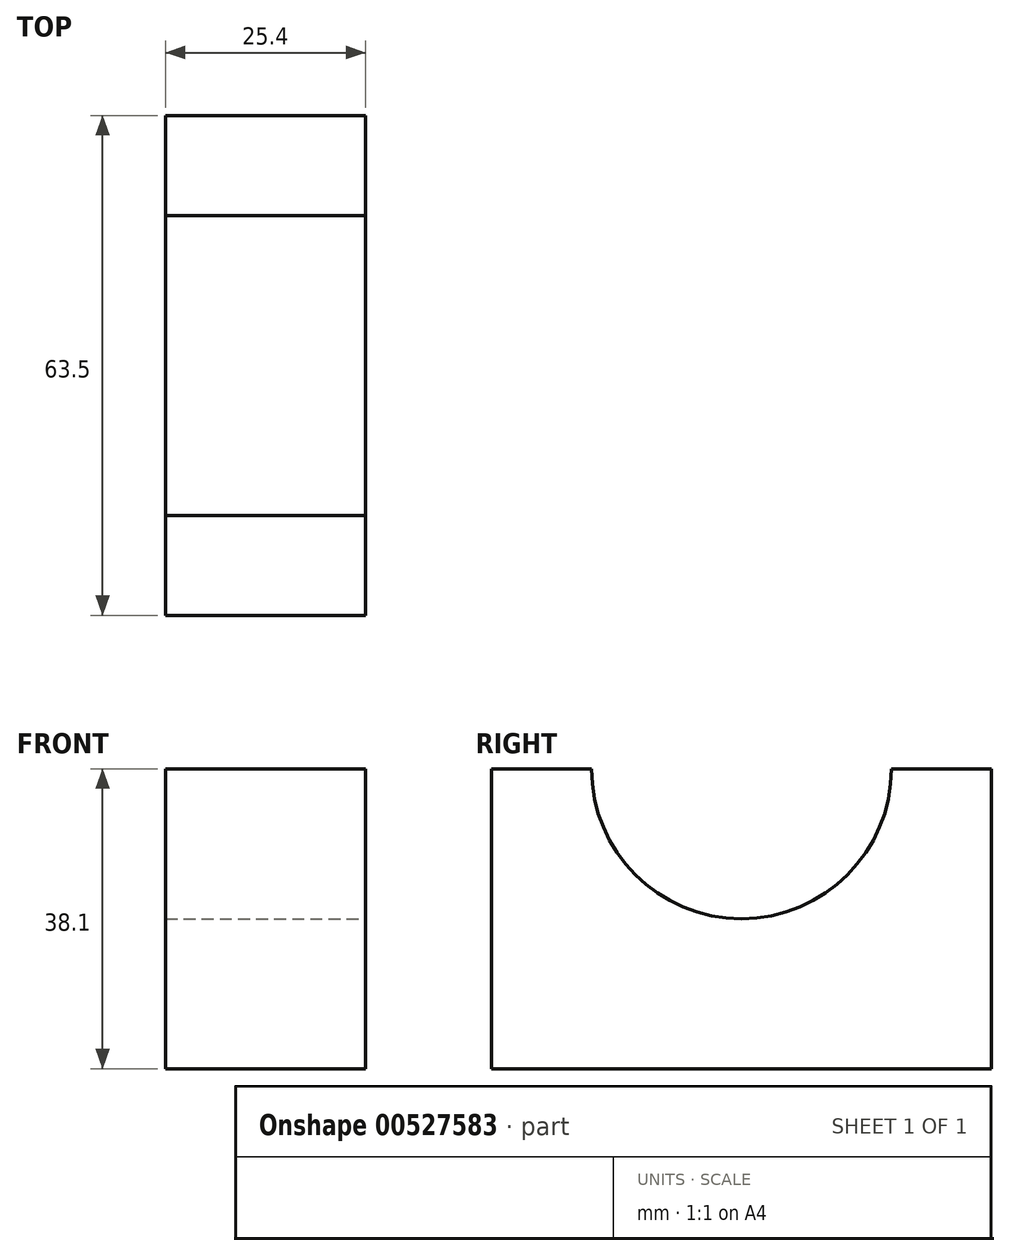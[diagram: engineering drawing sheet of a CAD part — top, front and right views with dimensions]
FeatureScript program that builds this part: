
annotation { "Feature Type Name" : "Feature", "Feature Type Description" : "" }
export const myFeature = defineFeature(function(context is Context, id is Id, definition is map)
    precondition{}
    {
        {
            var Q0;
            Q0=qCreatedBy(makeId("Front.planeOp"),FACE);
            var sketch = newSketch(context, id + "F0", { "sketchPlane" : qUnion([Q0])});
            skLineSegment(sketch, "E0", {"start": v(0, 0) * mm, "end": v(25.4, 0) * mm});
            skLineSegment(sketch, "E1", {"start": v(25.4, 0) * mm, "end": v(25.4, 38.1) * mm});
            skLineSegment(sketch, "E2", {"start": v(25.4, 38.1) * mm, "end": v(0, 38.1) * mm});
            skLineSegment(sketch, "E3", {"start": v(0, 38.1) * mm, "end": v(0, 0) * mm});
            skSolve(sketch);
        }
        {
            var Q0;
            Q0=makeQuery(id+"F0.imprint","IMPRINT",FACE,{"disambiguationData":[TD([[makeQuery(id+"F0.imprint","IMPRINT",EDGE,{"derivedFrom":sQuery(id+"F0.wireOp",EDGE,"E0")}),1.0]])]});
            extrude(context, id + "F1", {"entities" : qUnion([Q0]), "depth" : 63.5 * mm, "offsetDistance" : 25.4 * mm});
        }
        {
            var Q0;
            Q0=makeQuery(id+"F1.opExtrude","SWEPT_FACE",FACE,{"disambiguationData":[OSD([sQuery(id+"F0.wireOp",EDGE,"E1")])]});
            var sketch = newSketch(context, id + "F2", { "sketchPlane" : qUnion([Q0])});
            skCircle(sketch, "E4", {"center": v(-31.75, 38.1) * mm, "radius": 19.05 * mm});
            skSolve(sketch);
        }
        {
            var Q0;
            {var subQ0=sQuery(id+"F2.wireOp",EDGE,"E4");var subQ1=makeQuery(id+"F1.opExtrude","SWEPT_EDGE",EDGE,{"disambiguationData":[OSD([sQuery(id+"F0.wireOp",EDGE,"E1"),sQuery(id+"F0.wireOp",EDGE,"E2")])]});var subQ2=makeQuery(id+"F2.imprint","INTERSECT",VERTEX,{"disambiguationData":[OD(0.0)],"derivedFrom":[subQ1,subQ0]});Q0=makeQuery(id+"F2.imprint","IMPRINT",FACE,{"disambiguationData":[TD([[makeQuery(id+"F2.imprint","IMPRINT",EDGE,{"disambiguationData":[TD([[subQ2,1.0]])],"derivedFrom":subQ0}),1.0]])]});}
            extrude(context, id + "F3", {"entities" : qUnion([Q0]), "operationType" : NewBodyOperationType.REMOVE, "oppositeDirection" : true, "depth" : 25.4 * mm, "offsetDistance" : 25.4 * mm});
        }
    });
